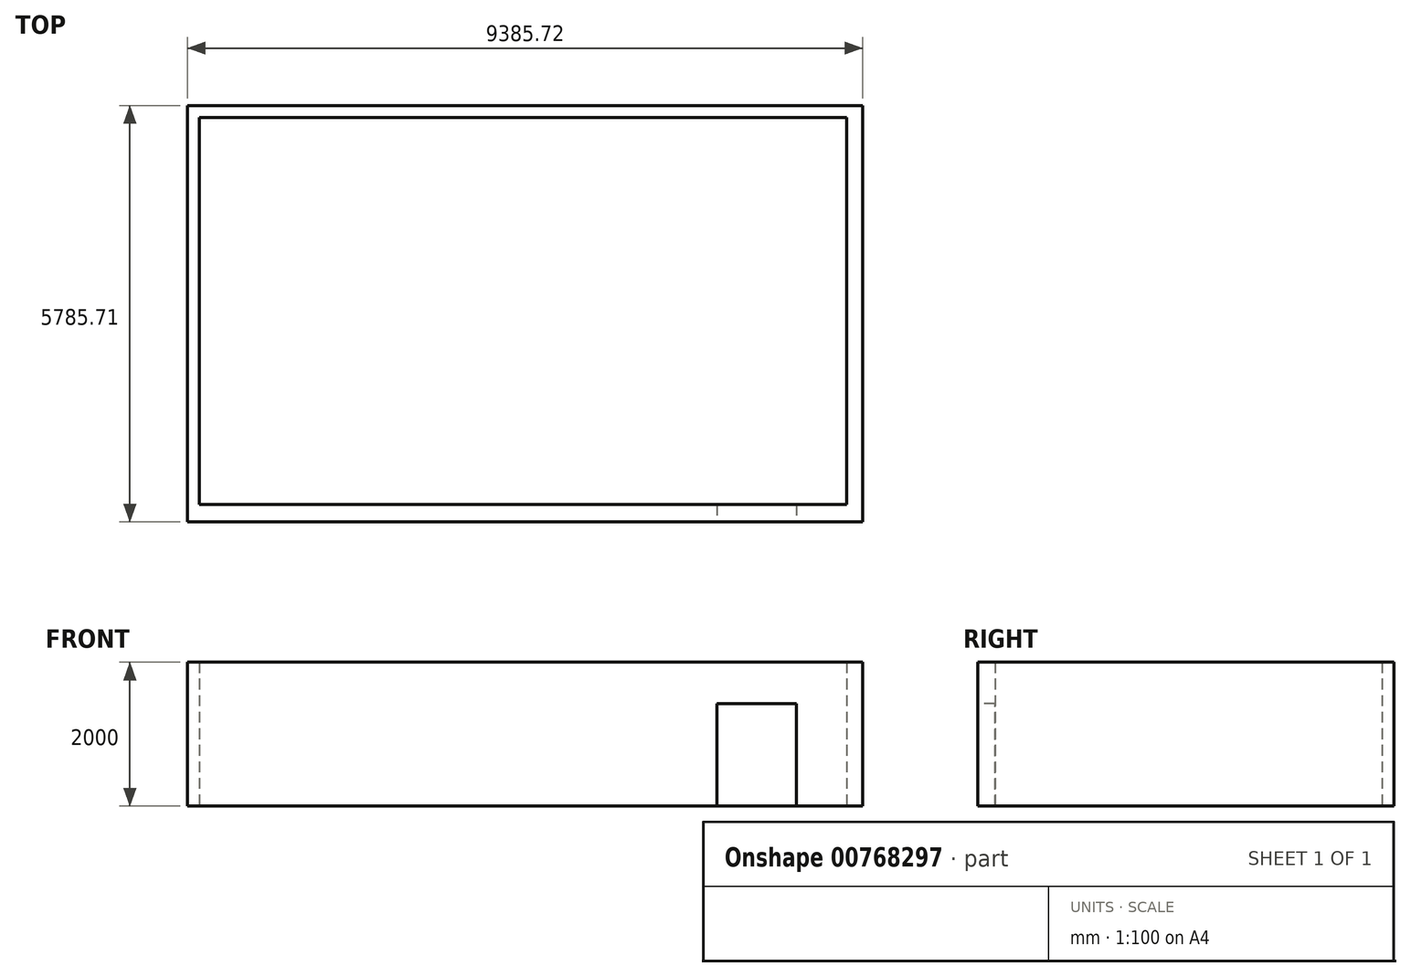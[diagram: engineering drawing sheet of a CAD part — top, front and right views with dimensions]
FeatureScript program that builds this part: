
annotation { "Feature Type Name" : "Feature", "Feature Type Description" : "" }
export const myFeature = defineFeature(function(context is Context, id is Id, definition is map)
    precondition{}
    {
        {
            var Q0;
            Q0=qCreatedBy(makeId("Top.planeOp"),FACE);
            var sketch = newSketch(context, id + "F0", { "sketchPlane" : qUnion([Q0])});
            skLineSegment(sketch, "E0.bottom", {"start": v(-4669.44, 2888.41) * mm, "end": v(4716.28, 2888.41) * mm});
            skLineSegment(sketch, "E0.top", {"start": v(-4669.44, -2897.3) * mm, "end": v(4716.28, -2897.3) * mm});
            skLineSegment(sketch, "E0.left", {"start": v(-4669.44, 2888.41) * mm, "end": v(-4669.44, -2897.3) * mm});
            skLineSegment(sketch, "E0.right", {"start": v(4716.28, 2888.41) * mm, "end": v(4716.28, -2897.3) * mm});
            skLineSegment(sketch, "E1.bottom", {"start": v(-4504.13, 2723.1) * mm, "end": v(4495.87, 2723.1) * mm});
            skLineSegment(sketch, "E1.top", {"start": v(-4504.13, -2658.53) * mm, "end": v(4495.87, -2658.53) * mm});
            skLineSegment(sketch, "E1.left", {"start": v(-4504.13, 2723.1) * mm, "end": v(-4504.13, -2658.53) * mm});
            skLineSegment(sketch, "E1.right", {"start": v(4495.87, 2723.1) * mm, "end": v(4495.87, -2658.53) * mm});
            skSolve(sketch);
        }
        {
            var Q0;
            Q0=makeQuery(id+"F0.imprint","IMPRINT",FACE,{"disambiguationData":[TD([[makeQuery(id+"F0.imprint","IMPRINT",EDGE,{"derivedFrom":sQuery(id+"F0.wireOp",EDGE,"E0.bottom")}),-1.0]])]});
            extrude(context, id + "F1", {"entities" : qUnion([Q0]), "depth" : 2000 * mm, "offsetDistance" : 25.4 * mm});
        }
        {
            var Q0;
            Q0=makeQuery(id+"F1.opExtrude","SWEPT_FACE",FACE,{"disambiguationData":[OSD([sQuery(id+"F0.wireOp",EDGE,"E0.top")])]});
            var sketch = newSketch(context, id + "F2", { "sketchPlane" : qUnion([Q0])});
            skLineSegment(sketch, "E2.bottom", {"start": v(2686.79, 1420.5) * mm, "end": v(3791.67, 1420.5) * mm});
            skLineSegment(sketch, "E2.top", {"start": v(2686.79, 0) * mm, "end": v(3791.67, 0) * mm});
            skLineSegment(sketch, "E2.left", {"start": v(2686.79, 1420.5) * mm, "end": v(2686.79, 0) * mm});
            skLineSegment(sketch, "E2.right", {"start": v(3791.67, 1420.5) * mm, "end": v(3791.67, 0) * mm});
            skSolve(sketch);
        }
        {
            var Q0;
            Q0=makeQuery(id+"F2.imprint","IMPRINT",FACE,{"disambiguationData":[TD([[makeQuery(id+"F2.imprint","IMPRINT",EDGE,{"derivedFrom":sQuery(id+"F2.wireOp",EDGE,"E2.bottom")}),-1.0]])]});
            extrude(context, id + "F3", {"entities" : qUnion([Q0]), "operationType" : NewBodyOperationType.REMOVE, "depth" : 25.4 * mm, "offsetDistance" : 25.4 * mm});
        }
        {
            var Q0;
            Q0 = qSketchRegion(id + "F2", true);
            extrude(context, id + "F4", {"entities" : qUnion([Q0]), "operationType" : NewBodyOperationType.REMOVE, "oppositeDirection" : true, "depth" : 1727.2 * mm, "offsetDistance" : 25.4 * mm});
        }
    });
